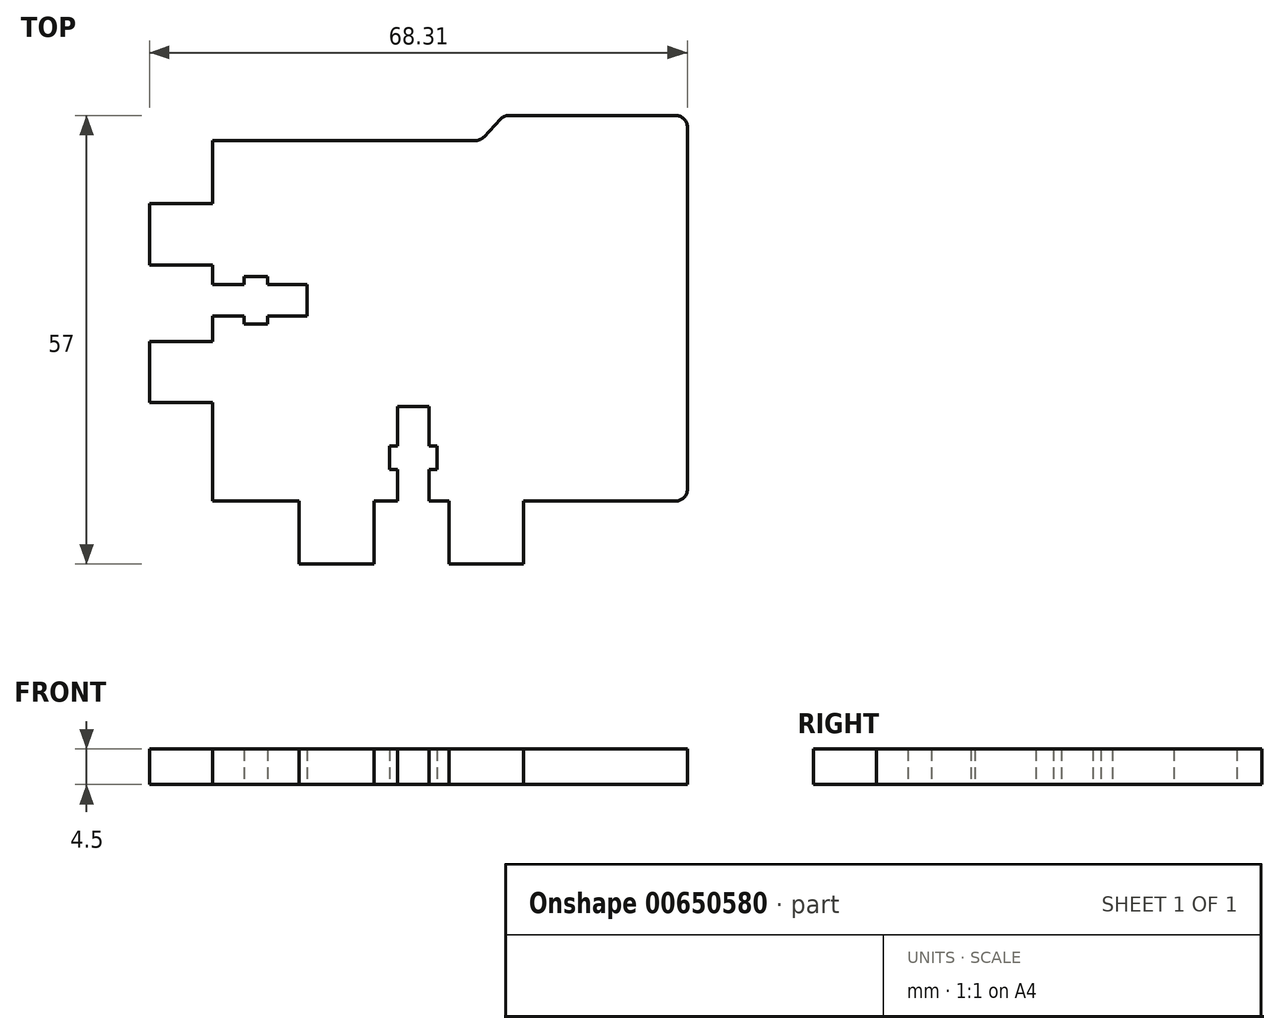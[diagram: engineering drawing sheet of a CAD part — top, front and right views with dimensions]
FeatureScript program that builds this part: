
annotation { "Feature Type Name" : "Feature", "Feature Type Description" : "" }
export const myFeature = defineFeature(function(context is Context, id is Id, definition is map)
    precondition{}
    {
        {
            var Q0;
            Q0=qCreatedBy(makeId("Top.planeOp"),FACE);
            var sketch = newSketch(context, id + "F0", { "sketchPlane" : qUnion([Q0])});
            skLineSegment(sketch, "E0", {"start": v(-19.56, 28.44) * mm, "end": v(13.8, 28.44) * mm});
            skLineSegment(sketch, "E1", {"start": v(14.89, 28.91) * mm, "end": v(17, 31.16) * mm});
            skLineSegment(sketch, "E2", {"start": v(18.1, 31.64) * mm, "end": v(39.25, 31.64) * mm});
            skLineSegment(sketch, "E3", {"start": v(40.75, 30.14) * mm, "end": v(40.75, -15.86) * mm});
            skLineSegment(sketch, "E4", {"start": v(39.25, -17.36) * mm, "end": v(19.94, -17.36) * mm});
            skLineSegment(sketch, "E5", {"start": v(19.94, -17.36) * mm, "end": v(19.94, -25.36) * mm});
            skLineSegment(sketch, "E6", {"start": v(19.94, -25.36) * mm, "end": v(10.44, -25.36) * mm});
            skLineSegment(sketch, "E7", {"start": v(10.44, -25.36) * mm, "end": v(10.44, -17.36) * mm});
            skLineSegment(sketch, "E8", {"start": v(10.44, -17.36) * mm, "end": v(7.94, -17.36) * mm});
            skLineSegment(sketch, "E9", {"start": v(7.94, -17.36) * mm, "end": v(7.94, -13.36) * mm});
            skLineSegment(sketch, "E10", {"start": v(7.94, -13.36) * mm, "end": v(8.94, -13.36) * mm});
            skLineSegment(sketch, "E11", {"start": v(8.94, -13.36) * mm, "end": v(8.94, -10.36) * mm});
            skLineSegment(sketch, "E12", {"start": v(8.94, -10.36) * mm, "end": v(7.94, -10.36) * mm});
            skLineSegment(sketch, "E13", {"start": v(7.94, -10.36) * mm, "end": v(7.94, -5.36) * mm});
            skLineSegment(sketch, "E14", {"start": v(7.94, -5.36) * mm, "end": v(3.94, -5.36) * mm});
            skLineSegment(sketch, "E15", {"start": v(3.94, -5.36) * mm, "end": v(3.94, -10.36) * mm});
            skLineSegment(sketch, "E16", {"start": v(3.94, -10.36) * mm, "end": v(2.94, -10.36) * mm});
            skLineSegment(sketch, "E17", {"start": v(2.94, -10.36) * mm, "end": v(2.94, -13.36) * mm});
            skLineSegment(sketch, "E18", {"start": v(2.94, -13.36) * mm, "end": v(3.94, -13.36) * mm});
            skLineSegment(sketch, "E19", {"start": v(3.94, -13.36) * mm, "end": v(3.94, -17.36) * mm});
            skLineSegment(sketch, "E20", {"start": v(3.94, -17.36) * mm, "end": v(0.94, -17.36) * mm});
            skLineSegment(sketch, "E21", {"start": v(0.94, -17.36) * mm, "end": v(0.94, -25.36) * mm});
            skLineSegment(sketch, "E22", {"start": v(0.94, -25.36) * mm, "end": v(-8.56, -25.36) * mm});
            skLineSegment(sketch, "E23", {"start": v(-8.56, -25.36) * mm, "end": v(-8.56, -17.36) * mm});
            skLineSegment(sketch, "E24", {"start": v(-8.56, -17.36) * mm, "end": v(-11.75, -17.36) * mm});
            skLineSegment(sketch, "E25", {"start": v(-19.56, -12.36) * mm, "end": v(-19.56, -4.86) * mm});
            skLineSegment(sketch, "E26", {"start": v(-19.56, -4.86) * mm, "end": v(-27.56, -4.86) * mm});
            skLineSegment(sketch, "E27", {"start": v(-27.56, -4.86) * mm, "end": v(-27.56, 2.94) * mm});
            skLineSegment(sketch, "E28", {"start": v(-27.56, 2.94) * mm, "end": v(-19.56, 2.94) * mm});
            skLineSegment(sketch, "E29", {"start": v(-19.56, 2.94) * mm, "end": v(-19.56, 6.14) * mm});
            skLineSegment(sketch, "E30", {"start": v(-19.56, 6.14) * mm, "end": v(-15.56, 6.14) * mm});
            skLineSegment(sketch, "E31", {"start": v(-15.56, 6.14) * mm, "end": v(-15.56, 5.14) * mm});
            skLineSegment(sketch, "E32", {"start": v(-15.56, 5.14) * mm, "end": v(-12.56, 5.14) * mm});
            skLineSegment(sketch, "E33", {"start": v(-12.56, 5.14) * mm, "end": v(-12.56, 6.14) * mm});
            skLineSegment(sketch, "E34", {"start": v(-12.56, 6.14) * mm, "end": v(-7.56, 6.14) * mm});
            skLineSegment(sketch, "E35", {"start": v(-7.56, 6.14) * mm, "end": v(-7.56, 10.14) * mm});
            skLineSegment(sketch, "E36", {"start": v(-7.56, 10.14) * mm, "end": v(-12.56, 10.14) * mm});
            skLineSegment(sketch, "E37", {"start": v(-12.56, 10.14) * mm, "end": v(-12.56, 11.14) * mm});
            skLineSegment(sketch, "E38", {"start": v(-12.56, 11.14) * mm, "end": v(-15.56, 11.14) * mm});
            skLineSegment(sketch, "E39", {"start": v(-15.56, 11.14) * mm, "end": v(-15.56, 10.14) * mm});
            skLineSegment(sketch, "E40", {"start": v(-15.56, 10.14) * mm, "end": v(-19.56, 10.14) * mm});
            skLineSegment(sketch, "E41", {"start": v(-19.56, 10.14) * mm, "end": v(-19.56, 12.64) * mm});
            skLineSegment(sketch, "E42", {"start": v(-19.56, 12.64) * mm, "end": v(-27.56, 12.64) * mm});
            skLineSegment(sketch, "E43", {"start": v(-27.56, 12.64) * mm, "end": v(-27.56, 20.44) * mm});
            skLineSegment(sketch, "E44", {"start": v(-27.56, 20.44) * mm, "end": v(-19.56, 20.44) * mm});
            skLineSegment(sketch, "E45", {"start": v(-19.56, 20.44) * mm, "end": v(-19.56, 28.44) * mm});
            skPoint(sketch, "E46.visualSharp", {"position": v(14.44, 28.44) * mm});
            skArc(sketch, "E46.filletArc", {"start": v(13.8, 28.44) * mm, "mid": v(14.39, 28.56) * mm, "end": v(14.89, 28.91) * mm});
            skPoint(sketch, "E47.visualSharp", {"position": v(17.44, 31.64) * mm});
            skArc(sketch, "E47.filletArc", {"start": v(18.1, 31.64) * mm, "mid": v(17.5, 31.52) * mm, "end": v(17, 31.16) * mm});
            skPoint(sketch, "E48.visualSharp", {"position": v(-19.56, -17.36) * mm});
            skLineSegment(sketch, "E49", {"start": v(-19.56, -12.36) * mm, "end": v(-19.56, -17.36) * mm});
            skLineSegment(sketch, "E50", {"start": v(-11.75, -17.36) * mm, "end": v(-19.56, -17.36) * mm});
            skPoint(sketch, "E51.visualSharp", {"position": v(40.75, 31.64) * mm});
            skArc(sketch, "E51.filletArc", {"start": v(40.75, 30.14) * mm, "mid": v(40.31, 31.2) * mm, "end": v(39.25, 31.64) * mm});
            skPoint(sketch, "E52.visualSharp", {"position": v(40.75, -17.36) * mm});
            skArc(sketch, "E52.filletArc", {"start": v(39.25, -17.36) * mm, "mid": v(40.31, -16.92) * mm, "end": v(40.75, -15.86) * mm});
            skSolve(sketch);
        }
        {
            var Q0;
            Q0=makeQuery(id+"F0.imprint","IMPRINT",FACE,{"disambiguationData":[TD([[makeQuery(id+"F0.imprint","IMPRINT",EDGE,{"derivedFrom":sQuery(id+"F0.wireOp",EDGE,"E0")}),-1.0]])]});
            extrude(context, id + "F1", {"entities" : qUnion([Q0]), "depth" : 4.5 * mm, "offsetDistance" : 25 * mm});
        }
    });
